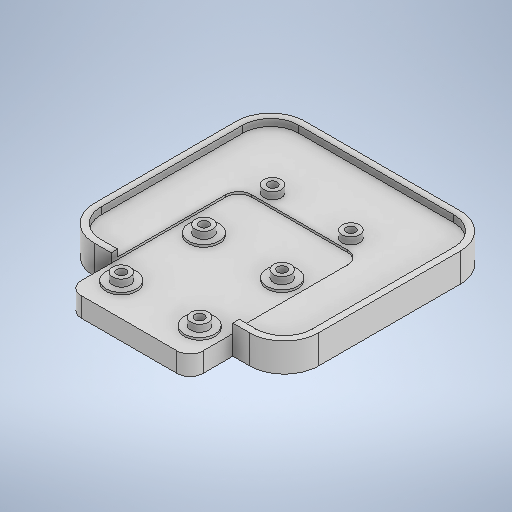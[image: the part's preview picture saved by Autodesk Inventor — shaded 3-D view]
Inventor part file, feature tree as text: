
AUTODESK INVENTOR PART (.ipt)
format: ipt  version: 2025 (Build 290162000, 162)  size: 402,432 bytes
history: native  units: mm
features: extrude x5, sketch x5, projected_geometry x2, shell x1
ambient origin geometry x8: Origin, YZ Plane, XZ Plane, XY Plane, X Axis, Y Axis, Z Axis, Center Point
bodies: Solid1 (feature_tree)
feature tree (13):
  extrude  "Extrusion1"  Depth=51.6mm
  shell  "Shell1"  Thickness=9.85mm
  extrude  "Extrusion2"  Depth=3.0mm
  extrude  "Extrusion3"  Depth=1.5mm
  extrude  "Extrusion4"  Depth=2.1mm
  extrude  "Extrusion5"  Depth=39.2mm
  sketch  "Sketch1"  dims[d0=48.5mm d1=51.6mm d2=9.85mm]
  sketch  "Sketch2"  dims[d3=28.0mm d5=3.0mm]
  sketch  "Sketch3"  dims[d6=5.0mm d7=0.0mm d8=1.5mm]
  sketch  "Sketch4"  dims[d10=8.0mm d11=2.1mm]
  sketch  "Sketch5"  dims[d12=18.0mm d13=15.8mm d14=19.0mm d15=0.0mm d16=0.0mm d17=1.5mm d18=1.6mm d19=0.0mm d20=4.0mm d21=1.6mm d22=0.0mm d25=7.0mm d26=0.5mm d27=0.0mm d30=39.2mm]
  projected_geometry  "Project Cut Edges1"
  projected_geometry  "Project Cut Edges2"
